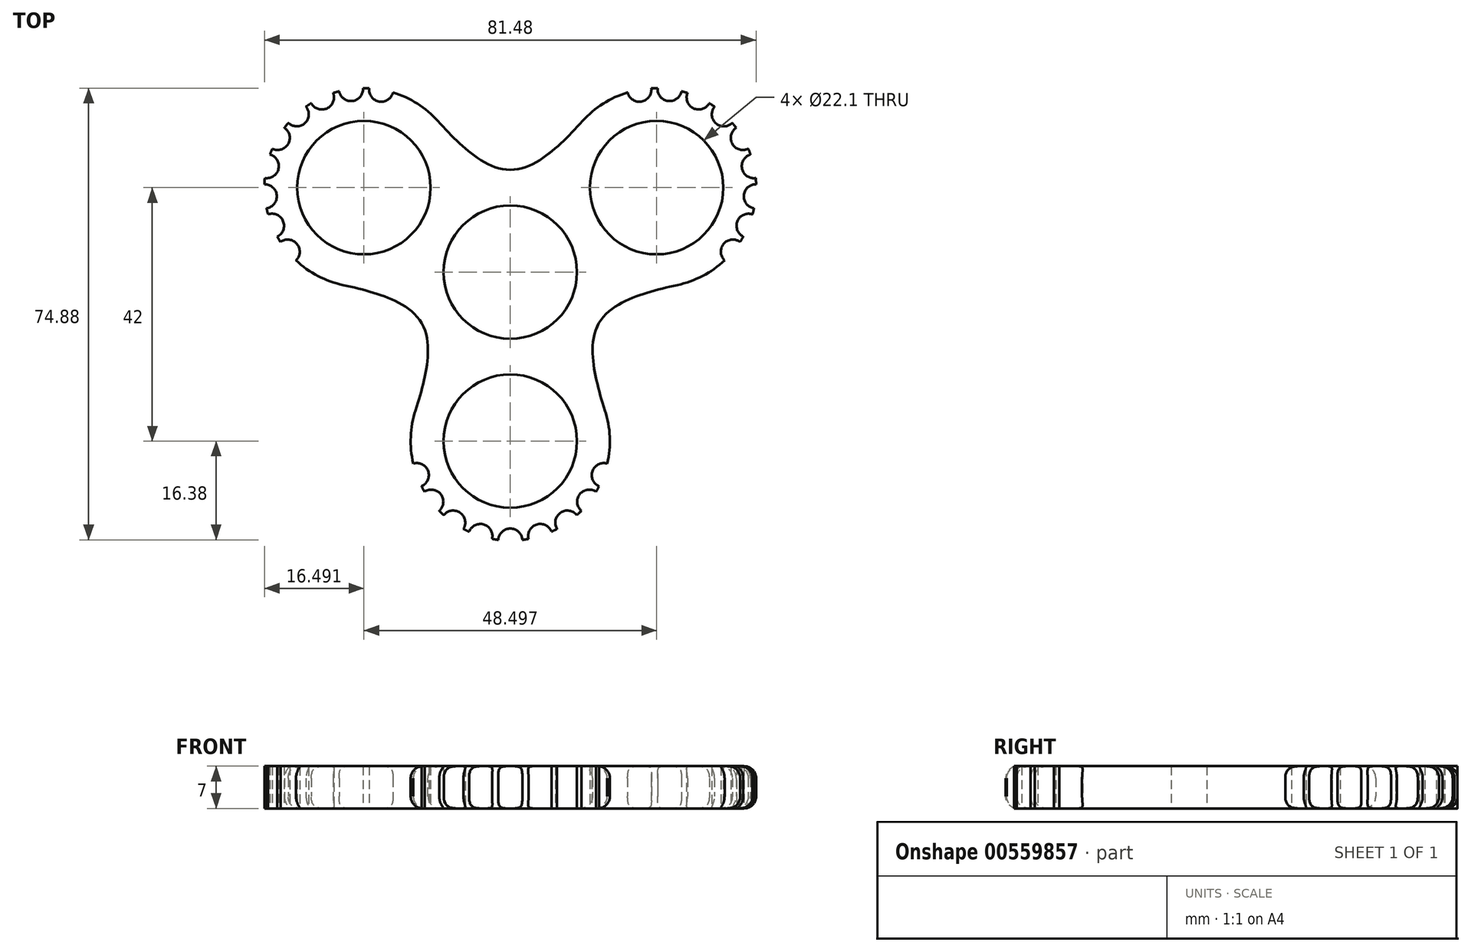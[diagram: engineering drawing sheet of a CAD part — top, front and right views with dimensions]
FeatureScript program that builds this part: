
annotation { "Feature Type Name" : "Feature", "Feature Type Description" : "" }
export const myFeature = defineFeature(function(context is Context, id is Id, definition is map)
    precondition{}
    {
        {
            var Q0;
            Q0=qCreatedBy(makeId("Top.planeOp"),FACE);
            var sketch = newSketch(context, id + "F0", { "sketchPlane" : qUnion([Q0])});
            skCircle(sketch, "E0", {"center": v(0, 0) * mm, "radius": 11.05 * mm});
            skCircle(sketch, "E1", {"center": v(-24.25, 14) * mm, "radius": 11.05 * mm});
            skCircle(sketch, "E2", {"center": v(24.25, 14) * mm, "radius": 11.05 * mm});
            skCircle(sketch, "E3", {"center": v(0, -28) * mm, "radius": 11.05 * mm});
            skLineSegment(sketch, "E4", {"start": v(-24.25, 14) * mm, "end": v(0, -28) * mm, "construction": true});
            skLineSegment(sketch, "E5", {"start": v(24.25, 14) * mm, "end": v(0, -28) * mm, "construction": true});
            skLineSegment(sketch, "E6", {"start": v(24.25, 14) * mm, "end": v(-24.25, 14) * mm, "construction": true});
            skLineSegment(sketch, "E7", {"start": v(0, 14) * mm, "end": v(0, 0) * mm, "construction": true});
            skLineSegment(sketch, "E8", {"start": v(0, 0) * mm, "end": v(12.12, -7) * mm, "construction": true});
            skLineSegment(sketch, "E9", {"start": v(0, 0) * mm, "end": v(-12.12, -7) * mm, "construction": true});
            skCircle(sketch, "E10", {"center": v(24.25, 14) * mm, "radius": 16.5 * mm});
            skCircle(sketch, "E11", {"center": v(-24.25, 14) * mm, "radius": 16.5 * mm});
            skCircle(sketch, "E12", {"center": v(0, -28) * mm, "radius": 16.5 * mm});
            skCircle(sketch, "E13", {"center": v(0, 0) * mm, "radius": 16.95 * mm, "construction": true});
            skLineSegment(sketch, "E14", {"start": v(-27.7, -2.14) * mm, "end": v(-15.7, -22.91) * mm, "construction": true});
            skLineSegment(sketch, "E15", {"start": v(15.7, -22.91) * mm, "end": v(27.7, -2.14) * mm, "construction": true});
            skLineSegment(sketch, "E16", {"start": v(12, 25.05) * mm, "end": v(-12, 25.05) * mm, "construction": true});
            skLineSegment(sketch, "E17", {"start": v(0, 0) * mm, "end": v(38.54, 22.25) * mm, "construction": true});
            skLineSegment(sketch, "E18", {"start": v(24.25, 14) * mm, "end": v(21.38, 30.25) * mm, "construction": true});
            skCircle(sketch, "E19", {"center": v(21.38, 30.25) * mm, "radius": 2 * mm});
            skCircle(sketch, "E20.1.0", {"center": v(26.4, 30.36) * mm, "radius": 2 * mm});
            skCircle(sketch, "E20.2.0", {"center": v(31.22, 28.95) * mm, "radius": 2 * mm});
            skCircle(sketch, "E20.3.0", {"center": v(35.4, 26.17) * mm, "radius": 2 * mm});
            skCircle(sketch, "E20.4.0", {"center": v(38.54, 22.25) * mm, "radius": 2 * mm});
            skCircle(sketch, "E20.5.0", {"center": v(40.36, 17.57) * mm, "radius": 2 * mm});
            skLineSegment(sketch, "E20.anchor2", {"start": v(24.25, 14) * mm, "end": v(36.89, 3.4) * mm, "construction": true});
            skCircle(sketch, "E21.1.0", {"center": v(-36.89, 3.4) * mm, "radius": 2 * mm});
            skCircle(sketch, "E21.1.1", {"center": v(-39.5, 7.69) * mm, "radius": 2 * mm});
            skCircle(sketch, "E21.1.2", {"center": v(-40.69, 12.56) * mm, "radius": 2 * mm});
            skCircle(sketch, "E21.1.3", {"center": v(-40.36, 17.57) * mm, "radius": 2 * mm});
            skCircle(sketch, "E21.1.4", {"center": v(-38.54, 22.25) * mm, "radius": 2 * mm});
            skCircle(sketch, "E21.1.5", {"center": v(-21.38, 30.25) * mm, "radius": 2 * mm});
            skCircle(sketch, "E21.2.0", {"center": v(15.5, -33.64) * mm, "radius": 2 * mm});
            skCircle(sketch, "E21.2.1", {"center": v(13.1, -38.04) * mm, "radius": 2 * mm});
            skCircle(sketch, "E21.2.2", {"center": v(9.46, -41.52) * mm, "radius": 2 * mm});
            skCircle(sketch, "E21.2.3", {"center": v(4.96, -43.74) * mm, "radius": 2 * mm});
            skCircle(sketch, "E21.2.4", {"center": v(0, -44.5) * mm, "radius": 2 * mm});
            skCircle(sketch, "E21.2.5", {"center": v(-15.5, -33.64) * mm, "radius": 2 * mm});
            skLineSegment(sketch, "E22", {"start": v(12.12, -7) * mm, "end": v(14.68, -8.47) * mm});
            skFitSpline(sketch, "E23", {"points": [v(27.7, -2.14) * mm, v(14.68, -8.47) * mm, v(15.7, -22.91) * mm], "startDerivative": vector(-34.49, -7.36) * mm, "endDerivative": vector(10.87, -33.55) * mm});
            skLineSegment(sketch, "E24", {"start": v(0, 14) * mm, "end": v(0, 16.95) * mm});
            skLineSegment(sketch, "E25", {"start": v(-12.12, -7) * mm, "end": v(-14.68, -8.48) * mm});
            skFitSpline(sketch, "E26", {"points": [v(-27.7, -2.14) * mm, v(-14.68, -8.48) * mm, v(-15.7, -22.91) * mm], "startDerivative": vector(34.49, -7.36) * mm, "endDerivative": vector(-10.87, -33.55) * mm});
            skFitSpline(sketch, "E27", {"points": [v(-12, 25.05) * mm, v(0, 16.95) * mm, v(12, 25.05) * mm], "startDerivative": vector(23.62, -26.19) * mm, "endDerivative": vector(23.62, 26.19) * mm});
            skCircle(sketch, "E28.1.6.0", {"center": v(40.69, 12.56) * mm, "radius": 2 * mm});
            skCircle(sketch, "E28.1.7.0", {"center": v(39.5, 7.69) * mm, "radius": 2 * mm});
            skCircle(sketch, "E28.1.8.0", {"center": v(36.89, 3.4) * mm, "radius": 2 * mm});
            skCircle(sketch, "E29.1.2", {"center": v(-26.4, 30.36) * mm, "radius": 2 * mm});
            skCircle(sketch, "E29.1.3", {"center": v(-31.22, 28.95) * mm, "radius": 2 * mm});
            skCircle(sketch, "E29.1.4", {"center": v(-35.4, 26.17) * mm, "radius": 2 * mm});
            skCircle(sketch, "E29.2.2", {"center": v(-13.1, -38.04) * mm, "radius": 2 * mm});
            skCircle(sketch, "E29.2.3", {"center": v(-9.46, -41.52) * mm, "radius": 2 * mm});
            skCircle(sketch, "E29.2.4", {"center": v(-4.96, -43.74) * mm, "radius": 2 * mm});
            skSolve(sketch);
        }
        {
            var Q0;
            Q0=makeQuery(id+"F0.imprint","IMPRINT",FACE,{"disambiguationData":[TD([[makeQuery(id+"F0.imprint","IMPRINT",EDGE,{"derivedFrom":sQuery(id+"F0.wireOp",EDGE,"E1")}),-1.0]])]});
            var Q1;
            Q1=makeQuery(id+"F0.imprint","IMPRINT",FACE,{"disambiguationData":[TD([[makeQuery(id+"F0.imprint","IMPRINT",EDGE,{"derivedFrom":sQuery(id+"F0.wireOp",EDGE,"E0")}),-1.0]])]});
            var Q2;
            Q2=makeQuery(id+"F0.imprint","IMPRINT",FACE,{"disambiguationData":[TD([[makeQuery(id+"F0.imprint","IMPRINT",EDGE,{"derivedFrom":sQuery(id+"F0.wireOp",EDGE,"E2")}),-1.0]])]});
            var Q3;
            Q3=makeQuery(id+"F0.imprint","IMPRINT",FACE,{"disambiguationData":[TD([[makeQuery(id+"F0.imprint","IMPRINT",EDGE,{"derivedFrom":sQuery(id+"F0.wireOp",EDGE,"E3")}),-1.0]])]});
            extrude(context, id + "F1", {"entities" : qUnion([Q0, Q1, Q2, Q3]), "depth" : 7 * mm, "offsetDistance" : 25 * mm});
        }
        {
            var Q0;
            Q0=makeQuery(id+"F1.opExtrude","CAP_FACE",FACE,{"disambiguationData":[OSD([sQuery(id+"F0.wireOp",EDGE,"E0"),sQuery(id+"F0.wireOp",EDGE,"E1"),sQuery(id+"F0.wireOp",EDGE,"E2"),sQuery(id+"F0.wireOp",EDGE,"E3"),sQuery(id+"F0.wireOp",EDGE,"E10"),sQuery(id+"F0.wireOp",EDGE,"E11"),sQuery(id+"F0.wireOp",EDGE,"E12"),sQuery(id+"F0.wireOp",EDGE,"8c590d80-f1ca-4e74-8db3-8beb0ea57340"),sQuery(id+"F0.wireOp",EDGE,"774baf55-adde-4f7b-879e-53019140c20c"),sQuery(id+"F0.wireOp",EDGE,"c6e45883-406c-416c-8891-a9c8438ed052"),sQuery(id+"F0.wireOp",EDGE,"E19"),sQuery(id+"F0.wireOp",EDGE,"E20.1.0"),sQuery(id+"F0.wireOp",EDGE,"E20.2.0"),sQuery(id+"F0.wireOp",EDGE,"E20.3.0"),sQuery(id+"F0.wireOp",EDGE,"E20.4.0"),sQuery(id+"F0.wireOp",EDGE,"E20.5.0"),sQuery(id+"F0.wireOp",EDGE,"E21.1.0"),sQuery(id+"F0.wireOp",EDGE,"E21.1.1"),sQuery(id+"F0.wireOp",EDGE,"E21.1.2"),sQuery(id+"F0.wireOp",EDGE,"E21.1.3"),sQuery(id+"F0.wireOp",EDGE,"E21.1.4"),sQuery(id+"F0.wireOp",EDGE,"E21.1.5"),sQuery(id+"F0.wireOp",EDGE,"E21.2.0"),sQuery(id+"F0.wireOp",EDGE,"E21.2.1"),sQuery(id+"F0.wireOp",EDGE,"E21.2.2"),sQuery(id+"F0.wireOp",EDGE,"E21.2.3"),sQuery(id+"F0.wireOp",EDGE,"E21.2.4"),sQuery(id+"F0.wireOp",EDGE,"E21.2.5")])],"isStart":false});
            var sketch = newSketch(context, id + "F2", { "sketchPlane" : qUnion([Q0])});
            skSolve(sketch);
        }
        {
            var Q0;
            {var subQ0=sQuery(id+"F0.wireOp",EDGE,"E11");Q0=makeQuery(id+"F1.opExtrude","CAP_EDGE",EDGE,{"disambiguationData":[OSD([subQ0]),TDD([makeQuery(id+"F0.imprint","IMPRINT",EDGE,{"disambiguationData":[TD([[makeQuery(id+"F0.imprint","INTERSECT",VERTEX,{"derivedFrom":[subQ0,sQuery(id+"F0.wireOp",EDGE,"E26")]}),1.0]])],"derivedFrom":subQ0})])],"isStart":true});}
            var Q1;
            Q1=makeQuery(id+"F1.opExtrude","CAP_EDGE",EDGE,{"disambiguationData":[OSD([sQuery(id+"F0.wireOp",EDGE,"E26")])],"isStart":true});
            var Q2;
            {var subQ0=sQuery(id+"F0.wireOp",EDGE,"E12");Q2=makeQuery(id+"F1.opExtrude","CAP_EDGE",EDGE,{"disambiguationData":[OSD([subQ0]),TDD([makeQuery(id+"F0.imprint","IMPRINT",EDGE,{"disambiguationData":[TD([[makeQuery(id+"F0.imprint","INTERSECT",VERTEX,{"derivedFrom":[subQ0,sQuery(id+"F0.wireOp",EDGE,"E26")]}),-1.0]])],"derivedFrom":subQ0})])],"isStart":true});}
            var Q3;
            {var subQ0=sQuery(id+"F0.wireOp",EDGE,"E12");Q3=makeQuery(id+"F1.opExtrude","CAP_EDGE",EDGE,{"disambiguationData":[OSD([subQ0]),TDD([makeQuery(id+"F0.imprint","IMPRINT",EDGE,{"disambiguationData":[TD([[makeQuery(id+"F0.imprint","INTERSECT",VERTEX,{"derivedFrom":[subQ0,sQuery(id+"F0.wireOp",EDGE,"E23")]}),1.0]])],"derivedFrom":subQ0})])],"isStart":true});}
            var Q4;
            Q4=makeQuery(id+"F1.opExtrude","CAP_EDGE",EDGE,{"disambiguationData":[OSD([sQuery(id+"F0.wireOp",EDGE,"E23")])],"isStart":true});
            var Q5;
            {var subQ0=sQuery(id+"F0.wireOp",EDGE,"E10");Q5=makeQuery(id+"F1.opExtrude","CAP_EDGE",EDGE,{"disambiguationData":[OSD([subQ0]),TDD([makeQuery(id+"F0.imprint","IMPRINT",EDGE,{"disambiguationData":[TD([[makeQuery(id+"F0.imprint","INTERSECT",VERTEX,{"derivedFrom":[subQ0,sQuery(id+"F0.wireOp",EDGE,"E23")]}),-1.0]])],"derivedFrom":subQ0})])],"isStart":true});}
            var Q6;
            {var subQ0=sQuery(id+"F0.wireOp",EDGE,"E10");Q6=makeQuery(id+"F1.opExtrude","CAP_EDGE",EDGE,{"disambiguationData":[OSD([subQ0]),TDD([makeQuery(id+"F0.imprint","IMPRINT",EDGE,{"disambiguationData":[TD([[makeQuery(id+"F0.imprint","INTERSECT",VERTEX,{"disambiguationData":[OD(1.0)],"derivedFrom":[subQ0,sQuery(id+"F0.wireOp",EDGE,"E28.1.8.0")]}),-1.0]])],"derivedFrom":subQ0})])],"isStart":true});}
            var Q7;
            {var subQ0=sQuery(id+"F0.wireOp",EDGE,"E10");Q7=makeQuery(id+"F1.opExtrude","CAP_EDGE",EDGE,{"disambiguationData":[OSD([subQ0]),TDD([makeQuery(id+"F0.imprint","IMPRINT",EDGE,{"disambiguationData":[TD([[makeQuery(id+"F0.imprint","INTERSECT",VERTEX,{"disambiguationData":[OD(1.0)],"derivedFrom":[subQ0,sQuery(id+"F0.wireOp",EDGE,"E28.1.7.0")]}),-1.0]])],"derivedFrom":subQ0})])],"isStart":true});}
            var Q8;
            {var subQ0=sQuery(id+"F0.wireOp",EDGE,"E10");Q8=makeQuery(id+"F1.opExtrude","CAP_EDGE",EDGE,{"disambiguationData":[OSD([subQ0]),TDD([makeQuery(id+"F0.imprint","IMPRINT",EDGE,{"disambiguationData":[TD([[makeQuery(id+"F0.imprint","INTERSECT",VERTEX,{"disambiguationData":[OD(0.0)],"derivedFrom":[subQ0,sQuery(id+"F0.wireOp",EDGE,"E20.5.0")]}),1.0]])],"derivedFrom":subQ0})])],"isStart":true});}
            var Q9;
            {var subQ0=sQuery(id+"F0.wireOp",EDGE,"E10");Q9=makeQuery(id+"F1.opExtrude","CAP_EDGE",EDGE,{"disambiguationData":[OSD([subQ0]),TDD([makeQuery(id+"F0.imprint","IMPRINT",EDGE,{"disambiguationData":[TD([[makeQuery(id+"F0.imprint","INTERSECT",VERTEX,{"disambiguationData":[OD(1.0)],"derivedFrom":[subQ0,sQuery(id+"F0.wireOp",EDGE,"E20.5.0")]}),-1.0]])],"derivedFrom":subQ0})])],"isStart":true});}
            var Q10;
            {var subQ0=sQuery(id+"F0.wireOp",EDGE,"E10");Q10=makeQuery(id+"F1.opExtrude","CAP_EDGE",EDGE,{"disambiguationData":[OSD([subQ0]),TDD([makeQuery(id+"F0.imprint","IMPRINT",EDGE,{"disambiguationData":[TD([[makeQuery(id+"F0.imprint","INTERSECT",VERTEX,{"disambiguationData":[OD(1.0)],"derivedFrom":[subQ0,sQuery(id+"F0.wireOp",EDGE,"E20.4.0")]}),-1.0]])],"derivedFrom":subQ0})])],"isStart":true});}
            var Q11;
            {var subQ0=sQuery(id+"F0.wireOp",EDGE,"E10");Q11=makeQuery(id+"F1.opExtrude","CAP_EDGE",EDGE,{"disambiguationData":[OSD([subQ0]),TDD([makeQuery(id+"F0.imprint","IMPRINT",EDGE,{"disambiguationData":[TD([[makeQuery(id+"F0.imprint","INTERSECT",VERTEX,{"disambiguationData":[OD(1.0)],"derivedFrom":[subQ0,sQuery(id+"F0.wireOp",EDGE,"E20.3.0")]}),-1.0]])],"derivedFrom":subQ0})])],"isStart":true});}
            var Q12;
            {var subQ0=sQuery(id+"F0.wireOp",EDGE,"E10");Q12=makeQuery(id+"F1.opExtrude","CAP_EDGE",EDGE,{"disambiguationData":[OSD([subQ0]),TDD([makeQuery(id+"F0.imprint","IMPRINT",EDGE,{"disambiguationData":[TD([[makeQuery(id+"F0.imprint","INTERSECT",VERTEX,{"disambiguationData":[OD(1.0)],"derivedFrom":[subQ0,sQuery(id+"F0.wireOp",EDGE,"E20.2.0")]}),-1.0]])],"derivedFrom":subQ0})])],"isStart":true});}
            var Q13;
            {var subQ0=sQuery(id+"F0.wireOp",EDGE,"E10");Q13=makeQuery(id+"F1.opExtrude","CAP_EDGE",EDGE,{"disambiguationData":[OSD([subQ0]),TDD([makeQuery(id+"F0.imprint","IMPRINT",EDGE,{"disambiguationData":[TD([[makeQuery(id+"F0.imprint","INTERSECT",VERTEX,{"disambiguationData":[OD(1.0)],"derivedFrom":[subQ0,sQuery(id+"F0.wireOp",EDGE,"E20.1.0")]}),-1.0]])],"derivedFrom":subQ0})])],"isStart":true});}
            var Q14;
            {var subQ0=sQuery(id+"F0.wireOp",EDGE,"E10");Q14=makeQuery(id+"F1.opExtrude","CAP_EDGE",EDGE,{"disambiguationData":[OSD([subQ0]),TDD([makeQuery(id+"F0.imprint","IMPRINT",EDGE,{"disambiguationData":[TD([[makeQuery(id+"F0.imprint","INTERSECT",VERTEX,{"derivedFrom":[subQ0,sQuery(id+"F0.wireOp",EDGE,"E27")]}),1.0]])],"derivedFrom":subQ0})])],"isStart":true});}
            var Q15;
            {var subQ0=sQuery(id+"F0.wireOp",EDGE,"E11");Q15=makeQuery(id+"F1.opExtrude","CAP_EDGE",EDGE,{"disambiguationData":[OSD([subQ0]),TDD([makeQuery(id+"F0.imprint","IMPRINT",EDGE,{"disambiguationData":[TD([[makeQuery(id+"F0.imprint","INTERSECT",VERTEX,{"disambiguationData":[OD(1.0)],"derivedFrom":[subQ0,sQuery(id+"F0.wireOp",EDGE,"E21.1.5")]}),-1.0]])],"derivedFrom":subQ0})])],"isStart":true});}
            var Q16;
            {var subQ0=sQuery(id+"F0.wireOp",EDGE,"E11");Q16=makeQuery(id+"F1.opExtrude","CAP_EDGE",EDGE,{"disambiguationData":[OSD([subQ0]),TDD([makeQuery(id+"F0.imprint","IMPRINT",EDGE,{"disambiguationData":[TD([[makeQuery(id+"F0.imprint","INTERSECT",VERTEX,{"disambiguationData":[OD(1.0)],"derivedFrom":[subQ0,sQuery(id+"F0.wireOp",EDGE,"E29.1.2")]}),-1.0]])],"derivedFrom":subQ0})])],"isStart":true});}
            var Q17;
            {var subQ0=sQuery(id+"F0.wireOp",EDGE,"E11");Q17=makeQuery(id+"F1.opExtrude","CAP_EDGE",EDGE,{"disambiguationData":[OSD([subQ0]),TDD([makeQuery(id+"F0.imprint","IMPRINT",EDGE,{"disambiguationData":[TD([[makeQuery(id+"F0.imprint","INTERSECT",VERTEX,{"disambiguationData":[OD(1.0)],"derivedFrom":[subQ0,sQuery(id+"F0.wireOp",EDGE,"E29.1.3")]}),-1.0]])],"derivedFrom":subQ0})])],"isStart":true});}
            var Q18;
            {var subQ0=sQuery(id+"F0.wireOp",EDGE,"E11");Q18=makeQuery(id+"F1.opExtrude","CAP_EDGE",EDGE,{"disambiguationData":[OSD([subQ0]),TDD([makeQuery(id+"F0.imprint","IMPRINT",EDGE,{"disambiguationData":[TD([[makeQuery(id+"F0.imprint","INTERSECT",VERTEX,{"disambiguationData":[OD(1.0)],"derivedFrom":[subQ0,sQuery(id+"F0.wireOp",EDGE,"E29.1.4")]}),-1.0]])],"derivedFrom":subQ0})])],"isStart":true});}
            var Q19;
            {var subQ0=sQuery(id+"F0.wireOp",EDGE,"E11");Q19=makeQuery(id+"F1.opExtrude","CAP_EDGE",EDGE,{"disambiguationData":[OSD([subQ0]),TDD([makeQuery(id+"F0.imprint","IMPRINT",EDGE,{"disambiguationData":[TD([[makeQuery(id+"F0.imprint","INTERSECT",VERTEX,{"disambiguationData":[OD(1.0)],"derivedFrom":[subQ0,sQuery(id+"F0.wireOp",EDGE,"E21.1.4")]}),-1.0]])],"derivedFrom":subQ0})])],"isStart":true});}
            var Q20;
            {var subQ0=sQuery(id+"F0.wireOp",EDGE,"E11");Q20=makeQuery(id+"F1.opExtrude","CAP_EDGE",EDGE,{"disambiguationData":[OSD([subQ0]),TDD([makeQuery(id+"F0.imprint","IMPRINT",EDGE,{"disambiguationData":[TD([[makeQuery(id+"F0.imprint","INTERSECT",VERTEX,{"disambiguationData":[OD(1.0)],"derivedFrom":[subQ0,sQuery(id+"F0.wireOp",EDGE,"E21.1.3")]}),-1.0]])],"derivedFrom":subQ0})])],"isStart":true});}
            var Q21;
            {var subQ0=sQuery(id+"F0.wireOp",EDGE,"E11");Q21=makeQuery(id+"F1.opExtrude","CAP_EDGE",EDGE,{"disambiguationData":[OSD([subQ0]),TDD([makeQuery(id+"F0.imprint","IMPRINT",EDGE,{"disambiguationData":[TD([[makeQuery(id+"F0.imprint","INTERSECT",VERTEX,{"disambiguationData":[OD(1.0)],"derivedFrom":[subQ0,sQuery(id+"F0.wireOp",EDGE,"E21.1.2")]}),-1.0]])],"derivedFrom":subQ0})])],"isStart":true});}
            var Q22;
            {var subQ0=sQuery(id+"F0.wireOp",EDGE,"E11");Q22=makeQuery(id+"F1.opExtrude","CAP_EDGE",EDGE,{"disambiguationData":[OSD([subQ0]),TDD([makeQuery(id+"F0.imprint","IMPRINT",EDGE,{"disambiguationData":[TD([[makeQuery(id+"F0.imprint","INTERSECT",VERTEX,{"disambiguationData":[OD(1.0)],"derivedFrom":[subQ0,sQuery(id+"F0.wireOp",EDGE,"E21.1.1")]}),-1.0]])],"derivedFrom":subQ0})])],"isStart":true});}
            var Q23;
            {var subQ0=sQuery(id+"F0.wireOp",EDGE,"E12");Q23=makeQuery(id+"F1.opExtrude","CAP_EDGE",EDGE,{"disambiguationData":[OSD([subQ0]),TDD([makeQuery(id+"F0.imprint","IMPRINT",EDGE,{"disambiguationData":[TD([[makeQuery(id+"F0.imprint","INTERSECT",VERTEX,{"disambiguationData":[OD(1.0)],"derivedFrom":[subQ0,sQuery(id+"F0.wireOp",EDGE,"E21.2.1")]}),-1.0]])],"derivedFrom":subQ0})])],"isStart":true});}
            var Q24;
            {var subQ0=sQuery(id+"F0.wireOp",EDGE,"E12");Q24=makeQuery(id+"F1.opExtrude","CAP_EDGE",EDGE,{"disambiguationData":[OSD([subQ0]),TDD([makeQuery(id+"F0.imprint","IMPRINT",EDGE,{"disambiguationData":[TD([[makeQuery(id+"F0.imprint","INTERSECT",VERTEX,{"disambiguationData":[OD(1.0)],"derivedFrom":[subQ0,sQuery(id+"F0.wireOp",EDGE,"E21.2.2")]}),-1.0]])],"derivedFrom":subQ0})])],"isStart":true});}
            var Q25;
            {var subQ0=sQuery(id+"F0.wireOp",EDGE,"E12");Q25=makeQuery(id+"F1.opExtrude","CAP_EDGE",EDGE,{"disambiguationData":[OSD([subQ0]),TDD([makeQuery(id+"F0.imprint","IMPRINT",EDGE,{"disambiguationData":[TD([[makeQuery(id+"F0.imprint","INTERSECT",VERTEX,{"disambiguationData":[OD(1.0)],"derivedFrom":[subQ0,sQuery(id+"F0.wireOp",EDGE,"E21.2.3")]}),-1.0]])],"derivedFrom":subQ0})])],"isStart":true});}
            var Q26;
            {var subQ0=sQuery(id+"F0.wireOp",EDGE,"E12");Q26=makeQuery(id+"F1.opExtrude","CAP_EDGE",EDGE,{"disambiguationData":[OSD([subQ0]),TDD([makeQuery(id+"F0.imprint","IMPRINT",EDGE,{"disambiguationData":[TD([[makeQuery(id+"F0.imprint","INTERSECT",VERTEX,{"disambiguationData":[OD(1.0)],"derivedFrom":[subQ0,sQuery(id+"F0.wireOp",EDGE,"E21.2.4")]}),-1.0]])],"derivedFrom":subQ0})])],"isStart":true});}
            var Q27;
            {var subQ0=sQuery(id+"F0.wireOp",EDGE,"E12");Q27=makeQuery(id+"F1.opExtrude","CAP_EDGE",EDGE,{"disambiguationData":[OSD([subQ0]),TDD([makeQuery(id+"F0.imprint","IMPRINT",EDGE,{"disambiguationData":[TD([[makeQuery(id+"F0.imprint","INTERSECT",VERTEX,{"disambiguationData":[OD(1.0)],"derivedFrom":[subQ0,sQuery(id+"F0.wireOp",EDGE,"E29.2.4")]}),-1.0]])],"derivedFrom":subQ0})])],"isStart":true});}
            var Q28;
            {var subQ0=sQuery(id+"F0.wireOp",EDGE,"E12");Q28=makeQuery(id+"F1.opExtrude","CAP_EDGE",EDGE,{"disambiguationData":[OSD([subQ0]),TDD([makeQuery(id+"F0.imprint","IMPRINT",EDGE,{"disambiguationData":[TD([[makeQuery(id+"F0.imprint","INTERSECT",VERTEX,{"disambiguationData":[OD(1.0)],"derivedFrom":[subQ0,sQuery(id+"F0.wireOp",EDGE,"E29.2.3")]}),-1.0]])],"derivedFrom":subQ0})])],"isStart":true});}
            var Q29;
            {var subQ0=sQuery(id+"F0.wireOp",EDGE,"E12");Q29=makeQuery(id+"F1.opExtrude","CAP_EDGE",EDGE,{"disambiguationData":[OSD([subQ0]),TDD([makeQuery(id+"F0.imprint","IMPRINT",EDGE,{"disambiguationData":[TD([[makeQuery(id+"F0.imprint","INTERSECT",VERTEX,{"disambiguationData":[OD(1.0)],"derivedFrom":[subQ0,sQuery(id+"F0.wireOp",EDGE,"E29.2.2")]}),-1.0]])],"derivedFrom":subQ0})])],"isStart":true});}
            var Q30;
            {var subQ0=sQuery(id+"F0.wireOp",EDGE,"E12");Q30=makeQuery(id+"F1.opExtrude","CAP_EDGE",EDGE,{"disambiguationData":[OSD([subQ0]),TDD([makeQuery(id+"F0.imprint","IMPRINT",EDGE,{"disambiguationData":[TD([[makeQuery(id+"F0.imprint","INTERSECT",VERTEX,{"disambiguationData":[OD(1.0)],"derivedFrom":[subQ0,sQuery(id+"F0.wireOp",EDGE,"E21.2.5")]}),-1.0]])],"derivedFrom":subQ0})])],"isStart":true});}
            var Q31;
            Q31=makeQuery(id+"F1.opExtrude","CAP_EDGE",EDGE,{"disambiguationData":[OSD([sQuery(id+"F0.wireOp",EDGE,"E27")])],"isStart":false});
            var Q32;
            Q32=makeQuery(id+"F1.opExtrude","CAP_EDGE",EDGE,{"disambiguationData":[OSD([sQuery(id+"F0.wireOp",EDGE,"E26")])],"isStart":false});
            var Q33;
            Q33=makeQuery(id+"F1.opExtrude","CAP_EDGE",EDGE,{"disambiguationData":[OSD([sQuery(id+"F0.wireOp",EDGE,"E23")])],"isStart":false});
            var Q34;
            {var subQ0=sQuery(id+"F0.wireOp",EDGE,"E11");Q34=makeQuery(id+"F1.opExtrude","CAP_EDGE",EDGE,{"disambiguationData":[OSD([subQ0]),TDD([makeQuery(id+"F0.imprint","IMPRINT",EDGE,{"disambiguationData":[TD([[makeQuery(id+"F0.imprint","INTERSECT",VERTEX,{"disambiguationData":[OD(1.0)],"derivedFrom":[subQ0,sQuery(id+"F0.wireOp",EDGE,"E21.1.5")]}),-1.0]])],"derivedFrom":subQ0})])],"isStart":false});}
            var Q35;
            {var subQ0=sQuery(id+"F0.wireOp",EDGE,"E11");Q35=makeQuery(id+"F1.opExtrude","CAP_EDGE",EDGE,{"disambiguationData":[OSD([subQ0]),TDD([makeQuery(id+"F0.imprint","IMPRINT",EDGE,{"disambiguationData":[TD([[makeQuery(id+"F0.imprint","INTERSECT",VERTEX,{"disambiguationData":[OD(1.0)],"derivedFrom":[subQ0,sQuery(id+"F0.wireOp",EDGE,"E29.1.2")]}),-1.0]])],"derivedFrom":subQ0})])],"isStart":false});}
            var Q36;
            {var subQ0=sQuery(id+"F0.wireOp",EDGE,"E11");Q36=makeQuery(id+"F1.opExtrude","CAP_EDGE",EDGE,{"disambiguationData":[OSD([subQ0]),TDD([makeQuery(id+"F0.imprint","IMPRINT",EDGE,{"disambiguationData":[TD([[makeQuery(id+"F0.imprint","INTERSECT",VERTEX,{"disambiguationData":[OD(1.0)],"derivedFrom":[subQ0,sQuery(id+"F0.wireOp",EDGE,"E29.1.3")]}),-1.0]])],"derivedFrom":subQ0})])],"isStart":false});}
            var Q37;
            {var subQ0=sQuery(id+"F0.wireOp",EDGE,"E11");Q37=makeQuery(id+"F1.opExtrude","CAP_EDGE",EDGE,{"disambiguationData":[OSD([subQ0]),TDD([makeQuery(id+"F0.imprint","IMPRINT",EDGE,{"disambiguationData":[TD([[makeQuery(id+"F0.imprint","INTERSECT",VERTEX,{"disambiguationData":[OD(1.0)],"derivedFrom":[subQ0,sQuery(id+"F0.wireOp",EDGE,"E29.1.4")]}),-1.0]])],"derivedFrom":subQ0})])],"isStart":false});}
            var Q38;
            {var subQ0=sQuery(id+"F0.wireOp",EDGE,"E11");Q38=makeQuery(id+"F1.opExtrude","CAP_EDGE",EDGE,{"disambiguationData":[OSD([subQ0]),TDD([makeQuery(id+"F0.imprint","IMPRINT",EDGE,{"disambiguationData":[TD([[makeQuery(id+"F0.imprint","INTERSECT",VERTEX,{"disambiguationData":[OD(1.0)],"derivedFrom":[subQ0,sQuery(id+"F0.wireOp",EDGE,"E21.1.4")]}),-1.0]])],"derivedFrom":subQ0})])],"isStart":false});}
            var Q39;
            {var subQ0=sQuery(id+"F0.wireOp",EDGE,"E11");Q39=makeQuery(id+"F1.opExtrude","CAP_EDGE",EDGE,{"disambiguationData":[OSD([subQ0]),TDD([makeQuery(id+"F0.imprint","IMPRINT",EDGE,{"disambiguationData":[TD([[makeQuery(id+"F0.imprint","INTERSECT",VERTEX,{"disambiguationData":[OD(1.0)],"derivedFrom":[subQ0,sQuery(id+"F0.wireOp",EDGE,"E21.1.3")]}),-1.0]])],"derivedFrom":subQ0})])],"isStart":false});}
            var Q40;
            {var subQ0=sQuery(id+"F0.wireOp",EDGE,"E11");Q40=makeQuery(id+"F1.opExtrude","CAP_EDGE",EDGE,{"disambiguationData":[OSD([subQ0]),TDD([makeQuery(id+"F0.imprint","IMPRINT",EDGE,{"disambiguationData":[TD([[makeQuery(id+"F0.imprint","INTERSECT",VERTEX,{"disambiguationData":[OD(1.0)],"derivedFrom":[subQ0,sQuery(id+"F0.wireOp",EDGE,"E21.1.2")]}),-1.0]])],"derivedFrom":subQ0})])],"isStart":false});}
            var Q41;
            {var subQ0=sQuery(id+"F0.wireOp",EDGE,"E11");Q41=makeQuery(id+"F1.opExtrude","CAP_EDGE",EDGE,{"disambiguationData":[OSD([subQ0]),TDD([makeQuery(id+"F0.imprint","IMPRINT",EDGE,{"disambiguationData":[TD([[makeQuery(id+"F0.imprint","INTERSECT",VERTEX,{"disambiguationData":[OD(1.0)],"derivedFrom":[subQ0,sQuery(id+"F0.wireOp",EDGE,"E21.1.1")]}),-1.0]])],"derivedFrom":subQ0})])],"isStart":false});}
            var Q42;
            {var subQ0=sQuery(id+"F0.wireOp",EDGE,"E10");Q42=makeQuery(id+"F1.opExtrude","CAP_EDGE",EDGE,{"disambiguationData":[OSD([subQ0]),TDD([makeQuery(id+"F0.imprint","IMPRINT",EDGE,{"disambiguationData":[TD([[makeQuery(id+"F0.imprint","INTERSECT",VERTEX,{"disambiguationData":[OD(1.0)],"derivedFrom":[subQ0,sQuery(id+"F0.wireOp",EDGE,"E20.1.0")]}),-1.0]])],"derivedFrom":subQ0})])],"isStart":false});}
            var Q43;
            {var subQ0=sQuery(id+"F0.wireOp",EDGE,"E10");Q43=makeQuery(id+"F1.opExtrude","CAP_EDGE",EDGE,{"disambiguationData":[OSD([subQ0]),TDD([makeQuery(id+"F0.imprint","IMPRINT",EDGE,{"disambiguationData":[TD([[makeQuery(id+"F0.imprint","INTERSECT",VERTEX,{"disambiguationData":[OD(1.0)],"derivedFrom":[subQ0,sQuery(id+"F0.wireOp",EDGE,"E20.2.0")]}),-1.0]])],"derivedFrom":subQ0})])],"isStart":false});}
            var Q44;
            {var subQ0=sQuery(id+"F0.wireOp",EDGE,"E10");Q44=makeQuery(id+"F1.opExtrude","CAP_EDGE",EDGE,{"disambiguationData":[OSD([subQ0]),TDD([makeQuery(id+"F0.imprint","IMPRINT",EDGE,{"disambiguationData":[TD([[makeQuery(id+"F0.imprint","INTERSECT",VERTEX,{"disambiguationData":[OD(1.0)],"derivedFrom":[subQ0,sQuery(id+"F0.wireOp",EDGE,"E20.3.0")]}),-1.0]])],"derivedFrom":subQ0})])],"isStart":false});}
            var Q45;
            {var subQ0=sQuery(id+"F0.wireOp",EDGE,"E10");Q45=makeQuery(id+"F1.opExtrude","CAP_EDGE",EDGE,{"disambiguationData":[OSD([subQ0]),TDD([makeQuery(id+"F0.imprint","IMPRINT",EDGE,{"disambiguationData":[TD([[makeQuery(id+"F0.imprint","INTERSECT",VERTEX,{"disambiguationData":[OD(1.0)],"derivedFrom":[subQ0,sQuery(id+"F0.wireOp",EDGE,"E20.4.0")]}),-1.0]])],"derivedFrom":subQ0})])],"isStart":false});}
            var Q46;
            {var subQ0=sQuery(id+"F0.wireOp",EDGE,"E10");Q46=makeQuery(id+"F1.opExtrude","CAP_EDGE",EDGE,{"disambiguationData":[OSD([subQ0]),TDD([makeQuery(id+"F0.imprint","IMPRINT",EDGE,{"disambiguationData":[TD([[makeQuery(id+"F0.imprint","INTERSECT",VERTEX,{"disambiguationData":[OD(1.0)],"derivedFrom":[subQ0,sQuery(id+"F0.wireOp",EDGE,"E20.5.0")]}),-1.0]])],"derivedFrom":subQ0})])],"isStart":false});}
            var Q47;
            {var subQ0=sQuery(id+"F0.wireOp",EDGE,"E10");Q47=makeQuery(id+"F1.opExtrude","CAP_EDGE",EDGE,{"disambiguationData":[OSD([subQ0]),TDD([makeQuery(id+"F0.imprint","IMPRINT",EDGE,{"disambiguationData":[TD([[makeQuery(id+"F0.imprint","INTERSECT",VERTEX,{"disambiguationData":[OD(0.0)],"derivedFrom":[subQ0,sQuery(id+"F0.wireOp",EDGE,"E20.5.0")]}),1.0]])],"derivedFrom":subQ0})])],"isStart":false});}
            var Q48;
            {var subQ0=sQuery(id+"F0.wireOp",EDGE,"E10");Q48=makeQuery(id+"F1.opExtrude","CAP_EDGE",EDGE,{"disambiguationData":[OSD([subQ0]),TDD([makeQuery(id+"F0.imprint","IMPRINT",EDGE,{"disambiguationData":[TD([[makeQuery(id+"F0.imprint","INTERSECT",VERTEX,{"disambiguationData":[OD(1.0)],"derivedFrom":[subQ0,sQuery(id+"F0.wireOp",EDGE,"E28.1.7.0")]}),-1.0]])],"derivedFrom":subQ0})])],"isStart":false});}
            var Q49;
            {var subQ0=sQuery(id+"F0.wireOp",EDGE,"E10");Q49=makeQuery(id+"F1.opExtrude","CAP_EDGE",EDGE,{"disambiguationData":[OSD([subQ0]),TDD([makeQuery(id+"F0.imprint","IMPRINT",EDGE,{"disambiguationData":[TD([[makeQuery(id+"F0.imprint","INTERSECT",VERTEX,{"disambiguationData":[OD(1.0)],"derivedFrom":[subQ0,sQuery(id+"F0.wireOp",EDGE,"E28.1.8.0")]}),-1.0]])],"derivedFrom":subQ0})])],"isStart":false});}
            var Q50;
            {var subQ0=sQuery(id+"F0.wireOp",EDGE,"E12");Q50=makeQuery(id+"F1.opExtrude","CAP_EDGE",EDGE,{"disambiguationData":[OSD([subQ0]),TDD([makeQuery(id+"F0.imprint","IMPRINT",EDGE,{"disambiguationData":[TD([[makeQuery(id+"F0.imprint","INTERSECT",VERTEX,{"disambiguationData":[OD(1.0)],"derivedFrom":[subQ0,sQuery(id+"F0.wireOp",EDGE,"E21.2.1")]}),-1.0]])],"derivedFrom":subQ0})])],"isStart":false});}
            var Q51;
            {var subQ0=sQuery(id+"F0.wireOp",EDGE,"E12");Q51=makeQuery(id+"F1.opExtrude","CAP_EDGE",EDGE,{"disambiguationData":[OSD([subQ0]),TDD([makeQuery(id+"F0.imprint","IMPRINT",EDGE,{"disambiguationData":[TD([[makeQuery(id+"F0.imprint","INTERSECT",VERTEX,{"disambiguationData":[OD(1.0)],"derivedFrom":[subQ0,sQuery(id+"F0.wireOp",EDGE,"E21.2.2")]}),-1.0]])],"derivedFrom":subQ0})])],"isStart":false});}
            var Q52;
            {var subQ0=sQuery(id+"F0.wireOp",EDGE,"E12");Q52=makeQuery(id+"F1.opExtrude","CAP_EDGE",EDGE,{"disambiguationData":[OSD([subQ0]),TDD([makeQuery(id+"F0.imprint","IMPRINT",EDGE,{"disambiguationData":[TD([[makeQuery(id+"F0.imprint","INTERSECT",VERTEX,{"disambiguationData":[OD(1.0)],"derivedFrom":[subQ0,sQuery(id+"F0.wireOp",EDGE,"E21.2.3")]}),-1.0]])],"derivedFrom":subQ0})])],"isStart":false});}
            var Q53;
            {var subQ0=sQuery(id+"F0.wireOp",EDGE,"E12");Q53=makeQuery(id+"F1.opExtrude","CAP_EDGE",EDGE,{"disambiguationData":[OSD([subQ0]),TDD([makeQuery(id+"F0.imprint","IMPRINT",EDGE,{"disambiguationData":[TD([[makeQuery(id+"F0.imprint","INTERSECT",VERTEX,{"disambiguationData":[OD(1.0)],"derivedFrom":[subQ0,sQuery(id+"F0.wireOp",EDGE,"E21.2.4")]}),-1.0]])],"derivedFrom":subQ0})])],"isStart":false});}
            var Q54;
            {var subQ0=sQuery(id+"F0.wireOp",EDGE,"E12");Q54=makeQuery(id+"F1.opExtrude","CAP_EDGE",EDGE,{"disambiguationData":[OSD([subQ0]),TDD([makeQuery(id+"F0.imprint","IMPRINT",EDGE,{"disambiguationData":[TD([[makeQuery(id+"F0.imprint","INTERSECT",VERTEX,{"disambiguationData":[OD(1.0)],"derivedFrom":[subQ0,sQuery(id+"F0.wireOp",EDGE,"E29.2.4")]}),-1.0]])],"derivedFrom":subQ0})])],"isStart":false});}
            var Q55;
            {var subQ0=sQuery(id+"F0.wireOp",EDGE,"E12");Q55=makeQuery(id+"F1.opExtrude","CAP_EDGE",EDGE,{"disambiguationData":[OSD([subQ0]),TDD([makeQuery(id+"F0.imprint","IMPRINT",EDGE,{"disambiguationData":[TD([[makeQuery(id+"F0.imprint","INTERSECT",VERTEX,{"disambiguationData":[OD(1.0)],"derivedFrom":[subQ0,sQuery(id+"F0.wireOp",EDGE,"E29.2.3")]}),-1.0]])],"derivedFrom":subQ0})])],"isStart":false});}
            var Q56;
            {var subQ0=sQuery(id+"F0.wireOp",EDGE,"E12");Q56=makeQuery(id+"F1.opExtrude","CAP_EDGE",EDGE,{"disambiguationData":[OSD([subQ0]),TDD([makeQuery(id+"F0.imprint","IMPRINT",EDGE,{"disambiguationData":[TD([[makeQuery(id+"F0.imprint","INTERSECT",VERTEX,{"disambiguationData":[OD(1.0)],"derivedFrom":[subQ0,sQuery(id+"F0.wireOp",EDGE,"E29.2.2")]}),-1.0]])],"derivedFrom":subQ0})])],"isStart":false});}
            var Q57;
            {var subQ0=sQuery(id+"F0.wireOp",EDGE,"E12");Q57=makeQuery(id+"F1.opExtrude","CAP_EDGE",EDGE,{"disambiguationData":[OSD([subQ0]),TDD([makeQuery(id+"F0.imprint","IMPRINT",EDGE,{"disambiguationData":[TD([[makeQuery(id+"F0.imprint","INTERSECT",VERTEX,{"disambiguationData":[OD(1.0)],"derivedFrom":[subQ0,sQuery(id+"F0.wireOp",EDGE,"E21.2.5")]}),-1.0]])],"derivedFrom":subQ0})])],"isStart":false});}
            fillet(context, id + "F3", {"entities" : qUnion([Q0, Q1, Q2, Q3, Q4, Q5, Q6, Q7, Q8, Q9, Q10, Q11, Q12, Q13, Q14, Q15, Q16, Q17, Q18, Q19, Q20, Q21, Q22, Q23, Q24, Q25, Q26, Q27, Q28, Q29, Q30, Q31, Q32, Q33, Q34, Q35, Q36, Q37, Q38, Q39, Q40, Q41, Q42, Q43, Q44, Q45, Q46, Q47, Q48, Q49, Q50, Q51, Q52, Q53, Q54, Q55, Q56, Q57]), "radius" : 2 * mm, "tangentPropagation" : true, "allowEdgeOverflow" : false});
        }
    });
